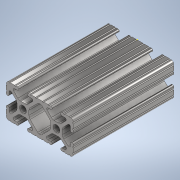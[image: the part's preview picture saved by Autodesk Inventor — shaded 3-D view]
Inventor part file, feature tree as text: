
AUTODESK INVENTOR PART (.ipt)
format: ipt  version: 2020 (Build 240168000, 168)  size: 346,112 bytes
history: native  units: in
note: dims shown in document units (in); Inventor stores cm internally (conversion verified against a paired STEP export)
features: sketch x2, extrude x1
ambient origin geometry x8: Origin, YZ Plane, XZ Plane, XY Plane, X Axis, Y Axis, Z Axis, Center Point
bodies: Solid1 (feature_tree)
feature tree (3):
  extrude  "Extrusion1"  [1 undecoded]
  sketch  "Sketch2"
  sketch  "Sketch1"  dims[d0=3.0in d1=0.0in]
note: 1 required parameter value undecoded (feature->parameter linkage not recoverable at this tier; creation-order binding heuristic only, values carry confidence <= 0.55)
